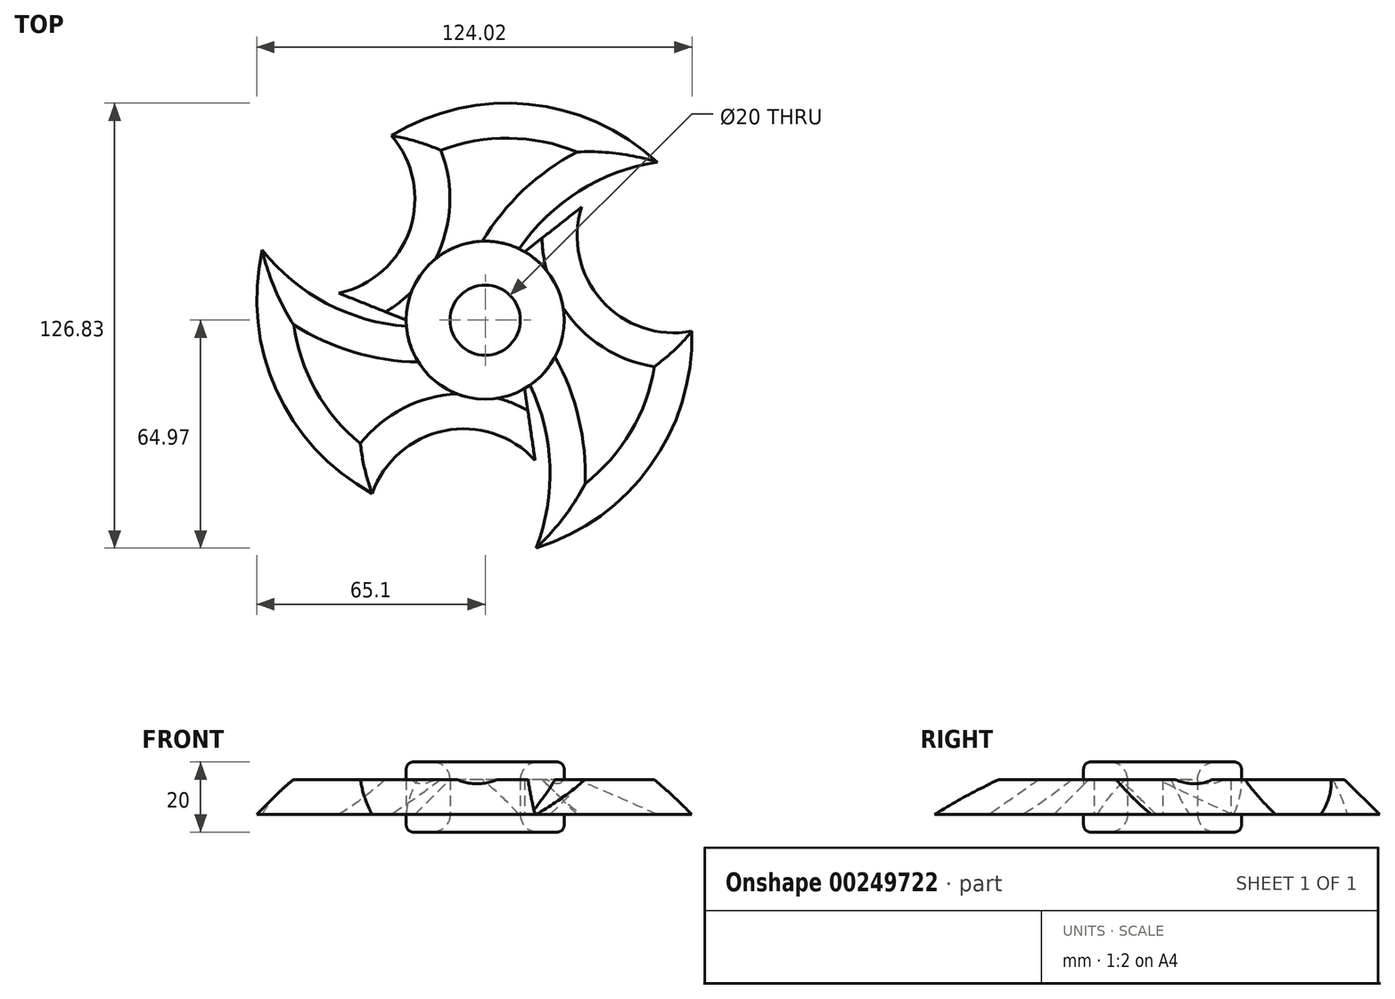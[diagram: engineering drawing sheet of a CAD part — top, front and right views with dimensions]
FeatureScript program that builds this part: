
annotation { "Feature Type Name" : "Feature", "Feature Type Description" : "" }
export const myFeature = defineFeature(function(context is Context, id is Id, definition is map)
    precondition{}
    {
        {
            var Q0;
            Q0=qCreatedBy(makeId("Top.planeOp"),FACE);
            var sketch = newSketch(context, id + "F0", { "sketchPlane" : qUnion([Q0])});
            skCircle(sketch, "E0", {"center": v(0, 0) * mm, "radius": 10 * mm});
            skCircle(sketch, "E1", {"center": v(0, 0) * mm, "radius": 22.5 * mm});
            skSolve(sketch);
        }
        {
            var Q0;
            Q0=makeQuery(id+"F0.imprint","IMPRINT",FACE,{"disambiguationData":[TD([[makeQuery(id+"F0.imprint","IMPRINT",EDGE,{"derivedFrom":sQuery(id+"F0.wireOp",EDGE,"E0")}),-1.0]])]});
            extrude(context, id + "F1", {"entities" : qUnion([Q0]), "depth" : 10 * mm, "hasSecondDirection" : true, "secondDirectionOppositeDirection" : true, "secondDirectionDepth" : 10 * mm});
        }
        {
            var Q0;
            Q0=makeQuery(id+"F1.opExtrude","CAP_EDGE",EDGE,{"disambiguationData":[OSD([sQuery(id+"F0.wireOp",EDGE,"E0")])],"isStart":false});
            fillet(context, id + "F2", {"entities" : qUnion([Q0]), "radius" : 5 * mm, "tangentPropagation" : true, "allowEdgeOverflow" : false});
        }
        {
            var Q0;
            Q0=qCreatedBy(makeId("Top.planeOp"),FACE);
            var sketch = newSketch(context, id + "F3", { "sketchPlane" : qUnion([Q0])});
            skCircle(sketch, "E2.0.0", {"center": v(0, 0) * mm, "radius": 22.5 * mm});
            skCircle(sketch, "E3.0.0", {"center": v(0, 0) * mm, "radius": 22.5 * mm, "construction": true});
            skArc(sketch, "E4", {"start": v(49.02, 45.04) * mm, "mid": v(26.77, 36.77) * mm, "end": v(9.67, 20.32) * mm});
            skArc(sketch, "E5", {"start": v(49.02, 45.04) * mm, "mid": v(12.43, 61.55) * mm, "end": v(-26.7, 52.6) * mm});
            skArc(sketch, "E6", {"start": v(-41.68, 7.67) * mm, "mid": v(-21.47, 25.9) * mm, "end": v(-26.7, 52.6) * mm});
            skLineSegment(sketch, "E7", {"start": v(-41.68, 7.67) * mm, "end": v(-22.5, 0) * mm});
            skArc(sketch, "E8.1.0", {"start": v(-63.51, 19.93) * mm, "mid": v(-45.23, 4.8) * mm, "end": v(-22.43, -1.78) * mm});
            skLineSegment(sketch, "E8.1.1", {"start": v(14.2, -39.93) * mm, "end": v(11.25, -19.49) * mm});
            skArc(sketch, "E8.1.2", {"start": v(14.2, -39.93) * mm, "mid": v(-11.69, -31.54) * mm, "end": v(-32.2, -49.42) * mm});
            skArc(sketch, "E8.1.3", {"start": v(-63.51, 19.93) * mm, "mid": v(-59.52, -20.01) * mm, "end": v(-32.2, -49.42) * mm});
            skArc(sketch, "E8.2.0", {"start": v(14.5, -64.97) * mm, "mid": v(18.46, -41.57) * mm, "end": v(12.76, -18.53) * mm});
            skLineSegment(sketch, "E8.2.1", {"start": v(27.48, 32.26) * mm, "end": v(11.25, 19.49) * mm});
            skArc(sketch, "E8.2.2", {"start": v(27.48, 32.26) * mm, "mid": v(33.16, 5.65) * mm, "end": v(58.9, -3.17) * mm});
            skArc(sketch, "E8.2.3", {"start": v(14.5, -64.97) * mm, "mid": v(47.1, -41.54) * mm, "end": v(58.9, -3.17) * mm});
            skSolve(sketch);
        }
        {
            var Q0;
            {var subQ0=sQuery(id+"F3.wireOp",EDGE,"E4");Q0=makeQuery(id+"F3.imprint","IMPRINT",FACE,{"disambiguationData":[TD([[makeQuery(id+"F3.imprint","IMPRINT",EDGE,{"derivedFrom":subQ0}),-1.0]])]});}
            var Q1;
            {var subQ1=sQuery(id+"F3.wireOp",EDGE,"E8.2.0");Q1=makeQuery(id+"F3.imprint","IMPRINT",FACE,{"disambiguationData":[TD([[makeQuery(id+"F3.imprint","IMPRINT",EDGE,{"derivedFrom":subQ1}),-1.0]])]});}
            var Q2;
            {var subQ0=sQuery(id+"F3.wireOp",EDGE,"E8.1.0");Q2=makeQuery(id+"F3.imprint","IMPRINT",FACE,{"disambiguationData":[TD([[makeQuery(id+"F3.imprint","IMPRINT",EDGE,{"derivedFrom":subQ0}),-1.0]])]});}
            extrude(context, id + "F4", {"entities" : qUnion([Q0, Q1, Q2]), "operationType" : NewBodyOperationType.ADD, "depth" : 5 * mm, "hasSecondDirection" : true, "secondDirectionOppositeDirection" : true, "secondDirectionDepth" : 5 * mm});
        }
        {
            var Q0;
            Q0=makeQuery(id+"F4.opExtrude","CAP_EDGE",EDGE,{"disambiguationData":[OSD([sQuery(id+"F3.wireOp",EDGE,"E8.1.0")])],"isStart":false});
            var Q1;
            Q1=makeQuery(id+"F4.opExtrude","CAP_EDGE",EDGE,{"disambiguationData":[OSD([sQuery(id+"F3.wireOp",EDGE,"E8.1.3")])],"isStart":false});
            var Q2;
            Q2=makeQuery(id+"F4.opExtrude","CAP_EDGE",EDGE,{"disambiguationData":[OSD([sQuery(id+"F3.wireOp",EDGE,"E8.1.2")])],"isStart":false});
            var Q3;
            Q3=makeQuery(id+"F4.opExtrude","CAP_EDGE",EDGE,{"disambiguationData":[OSD([sQuery(id+"F3.wireOp",EDGE,"E8.2.0")])],"isStart":false});
            var Q4;
            Q4=makeQuery(id+"F4.opExtrude","CAP_EDGE",EDGE,{"disambiguationData":[OSD([sQuery(id+"F3.wireOp",EDGE,"E8.2.3")])],"isStart":false});
            var Q5;
            Q5=makeQuery(id+"F4.opExtrude","CAP_EDGE",EDGE,{"disambiguationData":[OSD([sQuery(id+"F3.wireOp",EDGE,"E8.2.2")])],"isStart":false});
            var Q6;
            Q6=makeQuery(id+"F4.opExtrude","CAP_EDGE",EDGE,{"disambiguationData":[OSD([sQuery(id+"F3.wireOp",EDGE,"E6")])],"isStart":false});
            var Q7;
            Q7=makeQuery(id+"F4.opExtrude","CAP_EDGE",EDGE,{"disambiguationData":[OSD([sQuery(id+"F3.wireOp",EDGE,"E5")])],"isStart":false});
            var Q8;
            Q8=makeQuery(id+"F4.opExtrude","CAP_EDGE",EDGE,{"disambiguationData":[OSD([sQuery(id+"F3.wireOp",EDGE,"E4")])],"isStart":false});
            chamfer(context, id + "F5", {"entities" : qUnion([Q0, Q1, Q2, Q3, Q4, Q5, Q6, Q7, Q8]), "width" : 10 * mm, "tangentPropagation" : true});
        }
        {
            var Q0;
            Q0=makeQuery(id+"F1.opExtrude","CAP_EDGE",EDGE,{"disambiguationData":[OSD([sQuery(id+"F0.wireOp",EDGE,"E0")])],"isStart":true});
            fillet(context, id + "F6", {"entities" : qUnion([Q0]), "radius" : 5 * mm, "tangentPropagation" : true, "allowEdgeOverflow" : false});
        }
        {
            var Q0;
            Q0=makeQuery(id+"F1.opExtrude","CAP_EDGE",EDGE,{"disambiguationData":[OSD([sQuery(id+"F0.wireOp",EDGE,"E1")])],"isStart":false});
            var Q1;
            Q1=makeQuery(id+"F1.opExtrude","CAP_EDGE",EDGE,{"disambiguationData":[OSD([sQuery(id+"F0.wireOp",EDGE,"E1")])],"isStart":true});
            fillet(context, id + "F7", {"entities" : qUnion([Q0, Q1]), "radius" : 2 * mm, "tangentPropagation" : true, "allowEdgeOverflow" : false});
        }
    });
